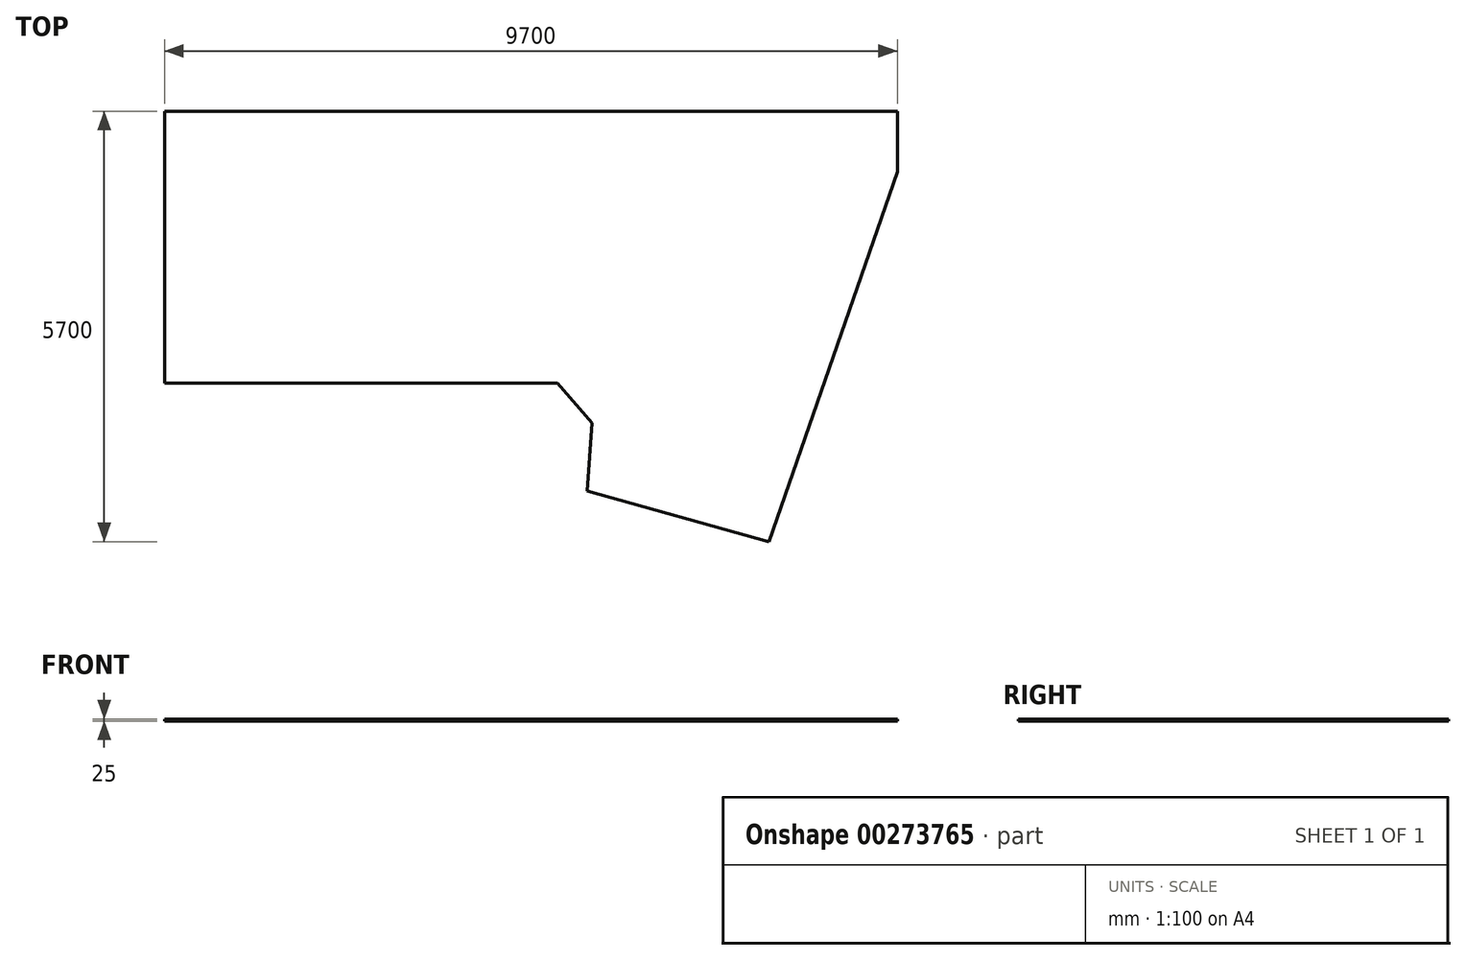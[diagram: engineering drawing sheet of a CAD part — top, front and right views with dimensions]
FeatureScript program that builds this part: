
annotation { "Feature Type Name" : "Feature", "Feature Type Description" : "" }
export const myFeature = defineFeature(function(context is Context, id is Id, definition is map)
    precondition{}
    {
        {
            var Q0;
            Q0=qCreatedBy(makeId("Top.planeOp"),FACE);
            var sketch = newSketch(context, id + "F0", { "sketchPlane" : qUnion([Q0])});
            skLineSegment(sketch, "E0.bottom", {"start": v(4850, -2850) * mm, "end": v(-4850, -2850) * mm});
            skLineSegment(sketch, "E0.top", {"start": v(4850, 2850) * mm, "end": v(-4850, 2850) * mm});
            skLineSegment(sketch, "E0.left", {"start": v(4850, -2850) * mm, "end": v(4850, 2850) * mm});
            skLineSegment(sketch, "E0.right", {"start": v(-4850, -2850) * mm, "end": v(-4850, 2850) * mm});
            skLineSegment(sketch, "E1.bottom", {"start": v(-4850, 2850) * mm, "end": v(350, 2850) * mm});
            skLineSegment(sketch, "E1.top", {"start": v(-4850, -750) * mm, "end": v(350, -750) * mm});
            skLineSegment(sketch, "E1.left", {"start": v(-4850, 2850) * mm, "end": v(-4850, -750) * mm});
            skLineSegment(sketch, "E2.bottom", {"start": v(-4850, 2850) * mm, "end": v(4850, 2850) * mm});
            skLineSegment(sketch, "E2.left", {"start": v(-4850, 2850) * mm, "end": v(-4850, 2050) * mm});
            skLineSegment(sketch, "E2.right", {"start": v(4850, 2850) * mm, "end": v(4850, 2050) * mm});
            skLineSegment(sketch, "E3.left", {"start": v(-4850, 2850) * mm, "end": v(-4850, -1280) * mm});
            skLineSegment(sketch, "E3.right", {"start": v(4850, 2850) * mm, "end": v(4850, -1280) * mm});
            skLineSegment(sketch, "E4", {"start": v(807.27, -1280) * mm, "end": v(350, -750) * mm});
            skLineSegment(sketch, "E5.bottom", {"start": v(4850, 2850) * mm, "end": v(3150, 2850) * mm});
            skLineSegment(sketch, "E5.top", {"start": v(4850, -2850) * mm, "end": v(3150, -2850) * mm});
            skLineSegment(sketch, "E5.left", {"start": v(4850, 2850) * mm, "end": v(4850, -2850) * mm});
            skLineSegment(sketch, "E6", {"start": v(3150, -2850) * mm, "end": v(4850, 2050) * mm});
            skPoint(sketch, "E7", {"position": v(742.11, -2177.64) * mm});
            skLineSegment(sketch, "E8", {"start": v(807.27, -1280) * mm, "end": v(742.11, -2177.64) * mm});
            skLineSegment(sketch, "E9", {"start": v(3150, -2850) * mm, "end": v(742.11, -2177.64) * mm});
            skSolve(sketch);
        }
        {
            var Q0;
            {var subQ1=sQuery(id+"F0.wireOp",EDGE,"E1.top");Q0=makeQuery(id+"F0.imprint","IMPRINT",FACE,{"disambiguationData":[TD([[makeQuery(id+"F0.imprint","IMPRINT",EDGE,{"derivedFrom":subQ1}),1.0]])]});}
            extrude(context, id + "F1", {"entities" : qUnion([Q0]), "depth" : 25 * mm});
        }
    });
